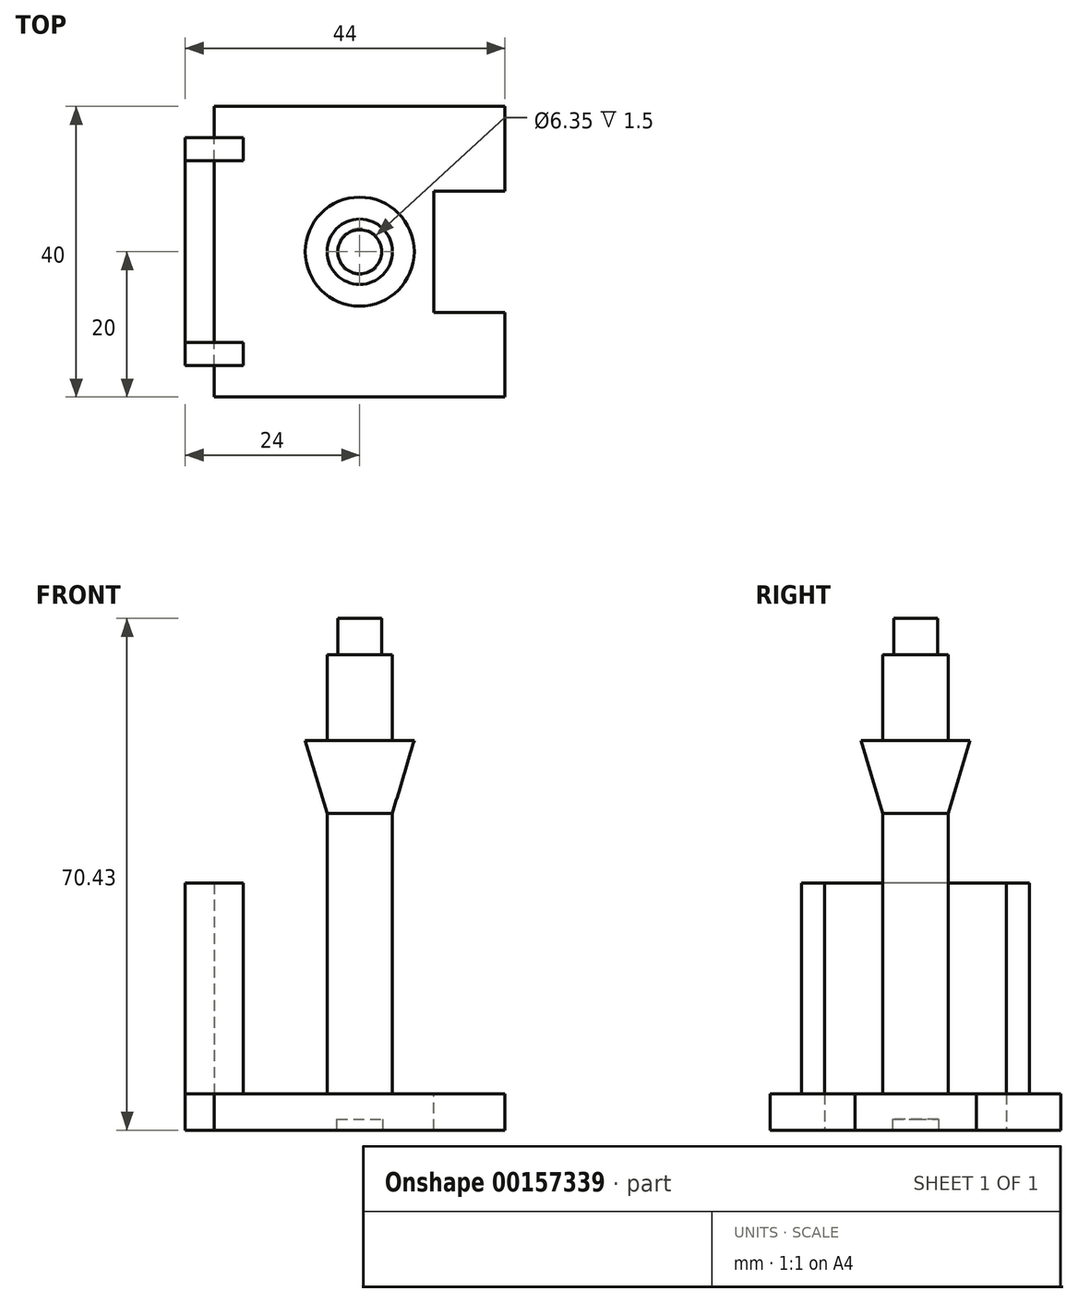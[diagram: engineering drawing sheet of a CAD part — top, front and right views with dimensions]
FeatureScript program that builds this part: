
annotation { "Feature Type Name" : "Feature", "Feature Type Description" : "" }
export const myFeature = defineFeature(function(context is Context, id is Id, definition is map)
    precondition{}
    {
        {
            var Q0;
            Q0=qCreatedBy(makeId("Top.planeOp"),FACE);
            var sketch = newSketch(context, id + "F0", { "sketchPlane" : qUnion([Q0])});
            skCircle(sketch, "E0", {"center": v(0, 0) * mm, "radius": 4.5 * mm});
            skSolve(sketch);
        }
        {
            var Q0;
            Q0=makeQuery(id+"F0.imprint","IMPRINT",FACE,{"disambiguationData":[TD([[makeQuery(id+"F0.imprint","IMPRINT",EDGE,{"derivedFrom":sQuery(id+"F0.wireOp",EDGE,"E0")}),1.0]])]});
            extrude(context, id + "F1", {"entities" : qUnion([Q0]), "depth" : 70.43 * mm});
        }
        {
            var Q0;
            Q0=makeQuery(id+"F1.opExtrude","CAP_FACE",FACE,{"disambiguationData":[OSD([sQuery(id+"F0.wireOp",EDGE,"E0")])],"isStart":false});
            var sketch = newSketch(context, id + "F2", { "sketchPlane" : qUnion([Q0])});
            skCircle(sketch, "E1", {"center": v(0, 0) * mm, "radius": 3.03 * mm});
            skCircle(sketch, "E2.0.0", {"center": v(0, 0) * mm, "radius": 4.5 * mm});
            skSolve(sketch);
        }
        {
            var Q0;
            Q0=makeQuery(id+"F2.imprint","IMPRINT",FACE,{"disambiguationData":[TD([[makeQuery(id+"F2.imprint","IMPRINT",EDGE,{"derivedFrom":sQuery(id+"F2.wireOp",EDGE,"E1")}),-1.0]])]});
            extrude(context, id + "F3", {"entities" : qUnion([Q0]), "operationType" : NewBodyOperationType.REMOVE, "oppositeDirection" : true, "depth" : 5 * mm});
        }
        {
            var Q0;
            Q0=makeQuery(id+"F1.opExtrude","CAP_FACE",FACE,{"disambiguationData":[OSD([sQuery(id+"F0.wireOp",EDGE,"E0")])],"isStart":true});
            var sketch = newSketch(context, id + "F4", { "sketchPlane" : qUnion([Q0])});
            skLineSegment(sketch, "E3.bottom", {"start": v(20, 20) * mm, "end": v(-20, 20) * mm});
            skLineSegment(sketch, "E3.top", {"start": v(20, -20) * mm, "end": v(-20, -20) * mm});
            skLineSegment(sketch, "E3.left", {"start": v(20, 20) * mm, "end": v(20, -20) * mm});
            skLineSegment(sketch, "E3.right", {"start": v(-20, 20) * mm, "end": v(-20, -20) * mm});
            skPoint(sketch, "E3.middle", {"position": v(0, 0) * mm});
            skSolve(sketch);
        }
        {
            var Q0;
            Q0=makeQuery(id+"F4.imprint","IMPRINT",FACE,{"disambiguationData":[TD([[makeQuery(id+"F4.imprint","IMPRINT",EDGE,{"derivedFrom":sQuery(id+"F4.wireOp",EDGE,"E3.bottom")}),1.0]])]});
            extrude(context, id + "F5", {"entities" : qUnion([Q0]), "operationType" : NewBodyOperationType.ADD, "oppositeDirection" : true, "depth" : 5 * mm});
        }
        {
            var Q0;
            Q0=makeQuery(id+"F5.opExtrude","SWEPT_FACE",FACE,{"disambiguationData":[OSD([sQuery(id+"F4.wireOp",EDGE,"E3.right")])]});
            var sketch = newSketch(context, id + "F6", { "sketchPlane" : qUnion([Q0])});
            skLineSegment(sketch, "E4.bottom", {"start": v(-12.5, 34) * mm, "end": v(12.5, 34) * mm});
            skLineSegment(sketch, "E4.top", {"start": v(-12.5, -34) * mm, "end": v(12.5, -34) * mm});
            skLineSegment(sketch, "E4.left", {"start": v(-12.5, 34) * mm, "end": v(-12.5, -34) * mm});
            skLineSegment(sketch, "E4.right", {"start": v(12.5, 34) * mm, "end": v(12.5, -34) * mm});
            skPoint(sketch, "E4.middle", {"position": v(0, 0) * mm});
            skLineSegment(sketch, "E5.1", {"start": v(20, 0) * mm, "end": v(-20, 0) * mm});
            skSolve(sketch);
        }
        {
            var Q0;
            {var subQ0=sQuery(id+"F6.wireOp",EDGE,"E4.bottom");Q0=makeQuery(id+"F6.imprint","IMPRINT",FACE,{"disambiguationData":[TD([[makeQuery(id+"F6.imprint","IMPRINT",EDGE,{"derivedFrom":subQ0}),-1.0]])]});}
            var Q1;
            {var subQ0=sQuery(id+"F6.wireOp",EDGE,"E5.1");var subQ1=sQuery(id+"F6.wireOp",EDGE,"E4.left");var subQ2=makeQuery(id+"F6.imprint","INTERSECT",VERTEX,{"derivedFrom":[subQ1,subQ0]});Q1=makeQuery(id+"F6.imprint","IMPRINT",FACE,{"disambiguationData":[TD([[makeQuery(id+"F6.imprint","IMPRINT",EDGE,{"disambiguationData":[TD([[subQ2,1.0]])],"derivedFrom":subQ1}),1.0]])]});}
            extrude(context, id + "F7", {"entities" : qUnion([Q0, Q1]), "operationType" : NewBodyOperationType.ADD, "depth" : 4 * mm});
        }
        {
            var Q0;
            {var subQ0=sQuery(id+"F4.wireOp",EDGE,"E3.top");var subQ1=sQuery(id+"F4.wireOp",EDGE,"E3.right");Q0=makeQuery(id+"F7.boolean.opBoolean","SPLIT",FACE,{"disambiguationData":[TD([makeQuery(id+"F5.opExtrude","SWEPT_FACE",FACE,{"disambiguationData":[OSD([subQ0])]})])],"derivedFrom":makeQuery(id+"F5.opExtrude","SWEPT_FACE",FACE,{"disambiguationData":[OSD([subQ1])]})});}
            var sketch = newSketch(context, id + "F8", { "sketchPlane" : qUnion([Q0])});
            skLineSegment(sketch, "E6.0.0", {"start": v(-12.5, 0) * mm, "end": v(-12.5, 5) * mm});
            skLineSegment(sketch, "E6.0.1", {"start": v(-12.5, 5) * mm, "end": v(-20, 5) * mm});
            skLineSegment(sketch, "E6.0.2", {"start": v(-20, 5) * mm, "end": v(-20, 0) * mm});
            skLineSegment(sketch, "E6.0.3", {"start": v(-20, 0) * mm, "end": v(-12.5, 0) * mm});
            skLineSegment(sketch, "E7.0.0", {"start": v(20, 5) * mm, "end": v(12.5, 5) * mm});
            skLineSegment(sketch, "E7.0.1", {"start": v(12.5, 5) * mm, "end": v(12.5, 0) * mm});
            skLineSegment(sketch, "E7.0.2", {"start": v(12.5, 0) * mm, "end": v(20, 0) * mm});
            skLineSegment(sketch, "E7.0.3", {"start": v(20, 0) * mm, "end": v(20, 5) * mm});
            skLineSegment(sketch, "E8.0.0", {"start": v(12.5, 34) * mm, "end": v(-12.5, 34) * mm});
            skLineSegment(sketch, "E8.0.1", {"start": v(-12.5, 34) * mm, "end": v(-12.5, 0) * mm});
            skLineSegment(sketch, "E8.0.2", {"start": v(-12.5, 0) * mm, "end": v(12.5, 0) * mm});
            skLineSegment(sketch, "E8.0.3", {"start": v(12.5, 0) * mm, "end": v(12.5, 34) * mm});
            skLineSegment(sketch, "E9.bottom", {"start": v(-12.5, 0) * mm, "end": v(-15.7, 0) * mm});
            skLineSegment(sketch, "E9.top", {"start": v(-12.5, 34) * mm, "end": v(-15.7, 34) * mm});
            skLineSegment(sketch, "E9.left", {"start": v(-12.5, 0) * mm, "end": v(-12.5, 34) * mm});
            skLineSegment(sketch, "E9.right", {"start": v(-15.7, 0) * mm, "end": v(-15.7, 34) * mm});
            skLineSegment(sketch, "E10.bottom", {"start": v(12.5, 0) * mm, "end": v(15.7, 0) * mm});
            skLineSegment(sketch, "E10.top", {"start": v(12.5, 34) * mm, "end": v(15.7, 34) * mm});
            skLineSegment(sketch, "E10.right", {"start": v(15.7, 0) * mm, "end": v(15.7, 34) * mm});
            skSolve(sketch);
        }
        {
            var Q0;
            {var subQ5=sQuery(id+"F8.wireOp",EDGE,"E9.top");Q0=makeQuery(id+"F8.imprint","IMPRINT",FACE,{"disambiguationData":[TD([[makeQuery(id+"F8.imprint","IMPRINT",EDGE,{"derivedFrom":subQ5}),1.0]])]});}
            var Q1;
            {var subQ5=sQuery(id+"F8.wireOp",EDGE,"E10.top");Q1=makeQuery(id+"F8.imprint","IMPRINT",FACE,{"disambiguationData":[TD([[makeQuery(id+"F8.imprint","IMPRINT",EDGE,{"derivedFrom":subQ5}),-1.0]])]});}
            var Q2;
            {var subQ5=sQuery(id+"F8.wireOp",EDGE,"E9.bottom");Q2=makeQuery(id+"F8.imprint","IMPRINT",FACE,{"disambiguationData":[TD([[makeQuery(id+"F8.imprint","IMPRINT",EDGE,{"derivedFrom":subQ5}),-1.0]])]});}
            var Q3;
            {var subQ5=sQuery(id+"F8.wireOp",EDGE,"E10.bottom");Q3=makeQuery(id+"F8.imprint","IMPRINT",FACE,{"disambiguationData":[TD([[makeQuery(id+"F8.imprint","IMPRINT",EDGE,{"derivedFrom":subQ5}),1.0]])]});}
            extrude(context, id + "F9", {"entities" : qUnion([Q0, Q1, Q2, Q3]), "endBound" : BoundingType.SYMMETRIC, "oppositeDirection" : true, "depth" : 8 * mm});
        }
        {
            var Q0;
            {var subQ0=sQuery(id+"F6.wireOp",EDGE,"E5.1");var subQ1=sQuery(id+"F0.wireOp",EDGE,"E0");Q0=makeQuery(id+"F6cNAdNJXaX2aCm_1.3.F7.boolean.opBoolean","MERGE",FACE,{"derivedFrom":[makeQuery(id+"F6cNAdNJXaX2aCm_1.2.F7.boolean.opBoolean","MERGE",FACE,{"derivedFrom":[makeQuery(id+"F6cNAdNJXaX2aCm_1.1.F7.boolean.opBoolean","MERGE",FACE,{"derivedFrom":[makeQuery(id+"F7.boolean.opBoolean","MERGE",FACE,{"derivedFrom":[makeQuery(id+"F5.boolean.opBoolean","MERGE",FACE,{"derivedFrom":[makeQuery(id+"F1.opExtrude","CAP_FACE",FACE,{"disambiguationData":[OSD([subQ1])],"isStart":true}),makeQuery(id+"F5.opExtrude","CAP_FACE",FACE,{"disambiguationData":[OSD([subQ1,sQuery(id+"F4.wireOp",EDGE,"E3.bottom"),sQuery(id+"F4.wireOp",EDGE,"E3.top"),sQuery(id+"F4.wireOp",EDGE,"E3.left"),sQuery(id+"F4.wireOp",EDGE,"E3.right")])],"isStart":true})]}),makeQuery(id+"F7.opExtrude","SWEPT_FACE",FACE,{"disambiguationData":[OSD([subQ0])]})]}),makeQuery(id+"F6cNAdNJXaX2aCm_1.1.F7.opExtrude","SWEPT_FACE",FACE,{"disambiguationData":[OSD([subQ0])]})]}),makeQuery(id+"F6cNAdNJXaX2aCm_1.2.F7.opExtrude","SWEPT_FACE",FACE,{"disambiguationData":[OSD([subQ0])]})]}),makeQuery(id+"F6cNAdNJXaX2aCm_1.3.F7.opExtrude","SWEPT_FACE",FACE,{"disambiguationData":[OSD([subQ0])]})]});}
            var sketch = newSketch(context, id + "F10", { "sketchPlane" : qUnion([Q0])});
            skPoint(sketch, "E11.0", {"position": v(0, 0) * mm});
            skCircle(sketch, "E12", {"center": v(0, 0) * mm, "radius": 3.18 * mm});
            skSolve(sketch);
        }
        {
            var Q0;
            Q0=makeQuery(id+"F10.imprint","IMPRINT",FACE,{"disambiguationData":[TD([[makeQuery(id+"F10.imprint","IMPRINT",EDGE,{"derivedFrom":sQuery(id+"F10.wireOp",EDGE,"E12")}),1.0]])]});
            extrude(context, id + "F11", {"entities" : qUnion([Q0]), "operationType" : NewBodyOperationType.REMOVE, "oppositeDirection" : true, "depth" : 1.5 * mm});
        }
        {
            var Q0;
            Q0=makeQuery(id+"F5.opExtrude","CAP_FACE",FACE,{"disambiguationData":[OSD([sQuery(id+"F0.wireOp",EDGE,"E0"),sQuery(id+"F4.wireOp",EDGE,"E3.bottom"),sQuery(id+"F4.wireOp",EDGE,"E3.top"),sQuery(id+"F4.wireOp",EDGE,"E3.left"),sQuery(id+"F4.wireOp",EDGE,"E3.right")])],"isStart":false});
            var sketch = newSketch(context, id + "F12", { "sketchPlane" : qUnion([Q0])});
            skLineSegment(sketch, "E13.0.0", {"start": v(20, -20) * mm, "end": v(20, -12.5) * mm});
            skLineSegment(sketch, "E13.0.1", {"start": v(20, -12.5) * mm, "end": v(20, 12.5) * mm});
            skLineSegment(sketch, "E13.0.2", {"start": v(20, 12.5) * mm, "end": v(20, 20) * mm});
            skLineSegment(sketch, "E13.0.3", {"start": v(20, 20) * mm, "end": v(12.5, 20) * mm});
            skLineSegment(sketch, "E13.0.4", {"start": v(12.5, 20) * mm, "end": v(-12.5, 20) * mm});
            skLineSegment(sketch, "E13.0.5", {"start": v(-12.5, 20) * mm, "end": v(-20, 20) * mm});
            skLineSegment(sketch, "E13.0.6", {"start": v(-20, 20) * mm, "end": v(-20, 12.5) * mm});
            skLineSegment(sketch, "E13.0.7", {"start": v(-20, 12.5) * mm, "end": v(-20, -12.5) * mm});
            skLineSegment(sketch, "E13.0.8", {"start": v(-20, -12.5) * mm, "end": v(-20, -20) * mm});
            skLineSegment(sketch, "E13.0.9", {"start": v(-20, -20) * mm, "end": v(-12.5, -20) * mm});
            skLineSegment(sketch, "E13.0.10", {"start": v(-12.5, -20) * mm, "end": v(12.5, -20) * mm});
            skLineSegment(sketch, "E13.0.11", {"start": v(12.5, -20) * mm, "end": v(20, -20) * mm});
            skLineSegment(sketch, "E14.bottom", {"start": v(20, 12.5) * mm, "end": v(9.2, 12.5) * mm});
            skLineSegment(sketch, "E14.top", {"start": v(20, -12.5) * mm, "end": v(9.2, -12.5) * mm});
            skLineSegment(sketch, "E14.left", {"start": v(20, 12.5) * mm, "end": v(20, -12.5) * mm});
            skLineSegment(sketch, "E15.bottom", {"start": v(20, 8.35) * mm, "end": v(10.2, 8.35) * mm});
            skLineSegment(sketch, "E15.top", {"start": v(20, -8.35) * mm, "end": v(10.2, -8.35) * mm});
            skLineSegment(sketch, "E15.left", {"start": v(20, 8.35) * mm, "end": v(20, -8.35) * mm});
            skLineSegment(sketch, "E15.right", {"start": v(10.2, 8.35) * mm, "end": v(10.2, -8.35) * mm});
            skSolve(sketch);
        }
        {
            var Q0;
            Q0=makeQuery(id+"F12.imprint","IMPRINT",FACE,{"disambiguationData":[TD([[makeQuery(id+"F12.imprint","IMPRINT",EDGE,{"derivedFrom":sQuery(id+"F12.wireOp",EDGE,"E15.bottom")}),1.0]])]});
            extrude(context, id + "F13", {"entities" : qUnion([Q0]), "operationType" : NewBodyOperationType.REMOVE, "oppositeDirection" : true, "depth" : 5 * mm});
        }
        {
            var Q0;
            Q0=qCreatedBy(makeId("Right.planeOp"),FACE);
            var sketch = newSketch(context, id + "F14", { "sketchPlane" : qUnion([Q0])});
            skLineSegment(sketch, "E16", {"start": v(-4.5, 5) * mm, "end": v(-4.5, 65.43) * mm});
            skLineSegment(sketch, "E17", {"start": v(4.5, 65.43) * mm, "end": v(4.5, 5) * mm});
            skLineSegment(sketch, "E18", {"start": v(0, 77.43) * mm, "end": v(0, -39.1) * mm});
            skSolve(sketch);
        }
        {
            var Q0;
            Q0=makeQuery(id+"F1.opExtrude","CAP_FACE",FACE,{"disambiguationData":[OSD([sQuery(id+"F0.wireOp",EDGE,"E0")])],"isStart":false});
            cPlane(context, id + "F15", {"entities" : qUnion([Q0]), "cplaneType" : CPlaneType.OFFSET, "offset" : 16.8 * mm, "oppositeDirection" : true, "width" : 150 * mm, "height" : 150 * mm});
        }
        {
            var Q0;
            Q0=qCreatedBy(id+"F15.planeOp",FACE);
            var sketch = newSketch(context, id + "F16", { "sketchPlane" : qUnion([Q0])});
            skCircle(sketch, "E19", {"center": v(0, 0) * mm, "radius": 7.5 * mm});
            skSolve(sketch);
        }
        {
            var Q0;
            Q0=makeQuery(id+"F1.opExtrude","CAP_FACE",FACE,{"disambiguationData":[OSD([sQuery(id+"F0.wireOp",EDGE,"E0")])],"isStart":false});
            cPlane(context, id + "F17", {"entities" : qUnion([Q0]), "cplaneType" : CPlaneType.OFFSET, "offset" : 26.8 * mm, "oppositeDirection" : true, "width" : 150 * mm, "height" : 150 * mm});
        }
        {
            var Q0;
            Q0=qCreatedBy(id+"F17.planeOp",FACE);
            var sketch = newSketch(context, id + "F18", { "sketchPlane" : qUnion([Q0])});
            skCircle(sketch, "E20.0", {"center": v(0, 0) * mm, "radius": 4.5 * mm});
            skSolve(sketch);
        }
        {
            var Q1;
            Q1=makeQuery(id+"F18.imprint","IMPRINT",FACE,{"disambiguationData":[TD([[makeQuery(id+"F18.imprint","IMPRINT",EDGE,{"derivedFrom":sQuery(id+"F18.wireOp",EDGE,"E20.0")}),1.0]])]});
            var Q2;
            Q2=makeQuery(id+"F16.imprint","IMPRINT",FACE,{"disambiguationData":[TD([[makeQuery(id+"F16.imprint","IMPRINT",EDGE,{"derivedFrom":sQuery(id+"F16.wireOp",EDGE,"E19")}),1.0]])]});
            loft(context, id + "F19", {"operationType" : NewBodyOperationType.ADD, "sheetProfilesArray" : [{ "sheetProfileEntities" : qUnion([Q1]) }, { "sheetProfileEntities" : qUnion([Q2]) }]});
        }
    });
